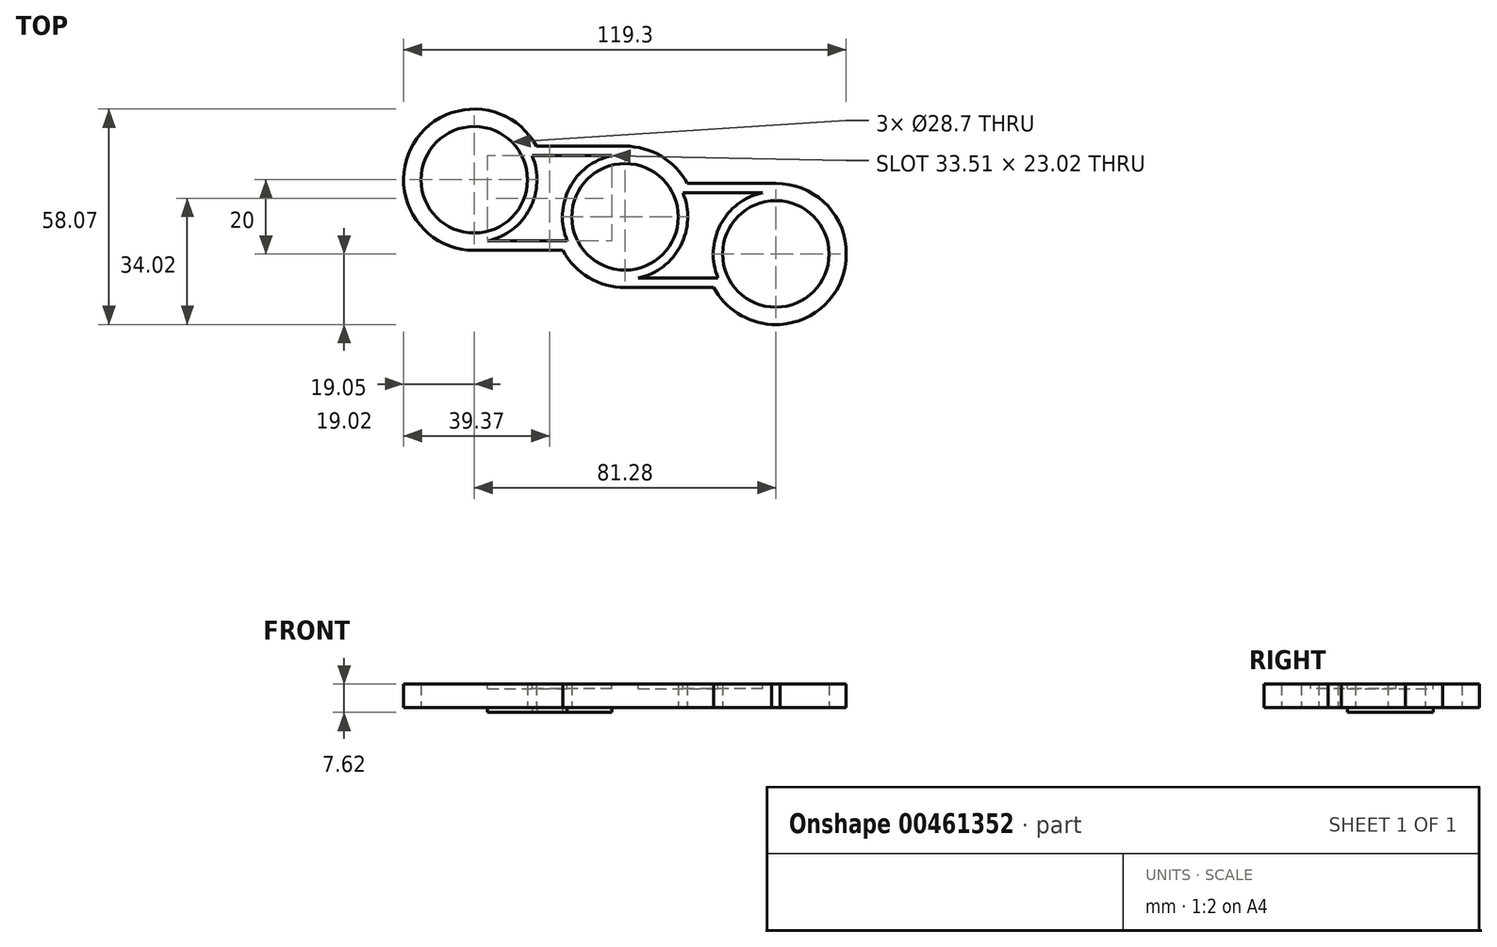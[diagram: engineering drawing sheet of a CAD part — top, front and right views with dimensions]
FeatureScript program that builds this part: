
annotation { "Feature Type Name" : "Feature", "Feature Type Description" : "" }
export const myFeature = defineFeature(function(context is Context, id is Id, definition is map)
    precondition{}
    {
        {
            var Q0;
            Q0=qCreatedBy(makeId("Top.planeOp"),FACE);
            var sketch = newSketch(context, id + "F0", { "sketchPlane" : qUnion([Q0])});
            skCircle(sketch, "E0", {"center": v(0, 0) * mm, "radius": 14.35 * mm});
            skCircle(sketch, "E1", {"center": v(40.64, -10) * mm, "radius": 14.35 * mm});
            skCircle(sketch, "E2", {"center": v(-40.64, 10) * mm, "radius": 14.35 * mm});
            skCircle(sketch, "E3", {"center": v(-40.64, 10) * mm, "radius": 19.05 * mm});
            skCircle(sketch, "E4", {"center": v(0, 0) * mm, "radius": 19.05 * mm});
            skCircle(sketch, "E5", {"center": v(40.64, -10) * mm, "radius": 19.05 * mm});
            skLineSegment(sketch, "E6", {"start": v(0, 19.05) * mm, "end": v(-23.88, 19.05) * mm});
            skLineSegment(sketch, "E7", {"start": v(-40.64, -9.05) * mm, "end": v(-16.76, -9.05) * mm});
            skLineSegment(sketch, "E8", {"start": v(0, -19.05) * mm, "end": v(23.88, -19.05) * mm});
            skLineSegment(sketch, "E9", {"start": v(40.64, 9.05) * mm, "end": v(16.76, 9.05) * mm});
            skLineSegment(sketch, "E10", {"start": v(-59.69, 10.15) * mm, "end": v(-59.69, 55.41) * mm});
            skLineSegment(sketch, "E11", {"start": v(59.6, -11.8) * mm, "end": v(59.6, 49.87) * mm});
            skLineSegment(sketch, "E12", {"start": v(-40.64, 29.05) * mm, "end": v(-1.94, 29.05) * mm});
            skLineSegment(sketch, "E13", {"start": v(41.8, -29.02) * mm, "end": v(-19.86, -29.02) * mm});
            skSolve(sketch);
        }
        {
            var Q0;
            Q0=makeQuery(id+"F0.imprint","IMPRINT",FACE,{"disambiguationData":[TD([[makeQuery(id+"F0.imprint","IMPRINT",EDGE,{"derivedFrom":sQuery(id+"F0.wireOp",EDGE,"E2")}),-1.0]])]});
            var Q1;
            {var subQ0=sQuery(id+"F0.wireOp",EDGE,"E6");Q1=makeQuery(id+"F0.imprint","IMPRINT",FACE,{"disambiguationData":[TD([[makeQuery(id+"F0.imprint","IMPRINT",EDGE,{"derivedFrom":subQ0}),1.0]])]});}
            var Q2;
            Q2=makeQuery(id+"F0.imprint","IMPRINT",FACE,{"disambiguationData":[TD([[makeQuery(id+"F0.imprint","IMPRINT",EDGE,{"derivedFrom":sQuery(id+"F0.wireOp",EDGE,"E0")}),-1.0]])]});
            var Q3;
            {var subQ0=sQuery(id+"F0.wireOp",EDGE,"E8");Q3=makeQuery(id+"F0.imprint","IMPRINT",FACE,{"disambiguationData":[TD([[makeQuery(id+"F0.imprint","IMPRINT",EDGE,{"derivedFrom":subQ0}),1.0]])]});}
            var Q4;
            Q4=makeQuery(id+"F0.imprint","IMPRINT",FACE,{"disambiguationData":[TD([[makeQuery(id+"F0.imprint","IMPRINT",EDGE,{"derivedFrom":sQuery(id+"F0.wireOp",EDGE,"E1")}),-1.0]])]});
            extrude(context, id + "F1", {"entities" : qUnion([Q0, Q1, Q2, Q3, Q4]), "depth" : 7.62 * mm});
        }
        {
            var Q0;
            Q0=makeQuery(id+"F1.opExtrude","CAP_FACE",FACE,{"disambiguationData":[OSD([sQuery(id+"F0.wireOp",EDGE,"E0"),sQuery(id+"F0.wireOp",EDGE,"E1"),sQuery(id+"F0.wireOp",EDGE,"E2"),sQuery(id+"F0.wireOp",EDGE,"E3"),sQuery(id+"F0.wireOp",EDGE,"E4"),sQuery(id+"F0.wireOp",EDGE,"E5"),sQuery(id+"F0.wireOp",EDGE,"E6"),sQuery(id+"F0.wireOp",EDGE,"E7"),sQuery(id+"F0.wireOp",EDGE,"E8"),sQuery(id+"F0.wireOp",EDGE,"E9")])],"isStart":false});
            shell(context, id + "F2", {"entities" : qUnion([Q0]), "thickness" : 2.54 * mm});
        }
        {
            var Q0;
            Q0=makeQuery(id+"F1.opExtrude","CAP_FACE",FACE,{"disambiguationData":[OSD([sQuery(id+"F0.wireOp",EDGE,"E0"),sQuery(id+"F0.wireOp",EDGE,"E1"),sQuery(id+"F0.wireOp",EDGE,"E2"),sQuery(id+"F0.wireOp",EDGE,"E3"),sQuery(id+"F0.wireOp",EDGE,"E4"),sQuery(id+"F0.wireOp",EDGE,"E5"),sQuery(id+"F0.wireOp",EDGE,"E6"),sQuery(id+"F0.wireOp",EDGE,"E7"),sQuery(id+"F0.wireOp",EDGE,"E8"),sQuery(id+"F0.wireOp",EDGE,"E9")])],"isStart":false});
            var sketch = newSketch(context, id + "F3", { "sketchPlane" : qUnion([Q0])});
            skLineSegment(sketch, "E14.0", {"start": v(-3.57, 16.51) * mm, "end": v(-25.05, 16.5) * mm});
            skArc(sketch, "E14.1", {"start": v(-37.07, -6.5) * mm, "mid": v(-25.67, 2.18) * mm, "end": v(-25.05, 16.5) * mm});
            skLineSegment(sketch, "E14.2", {"start": v(-37.07, -6.5) * mm, "end": v(-15.59, -6.5) * mm});
            skArc(sketch, "E14.3", {"start": v(-3.57, 16.51) * mm, "mid": v(-14.97, 7.82) * mm, "end": v(-15.59, -6.5) * mm});
            skLineSegment(sketch, "E14.4", {"start": v(37.07, 6.51) * mm, "end": v(15.59, 6.5) * mm});
            skArc(sketch, "E14.5", {"start": v(3.57, -16.51) * mm, "mid": v(14.97, -7.82) * mm, "end": v(15.59, 6.5) * mm});
            skArc(sketch, "E14.6", {"start": v(37.07, 6.5) * mm, "mid": v(25.67, -2.18) * mm, "end": v(25.05, -16.5) * mm});
            skLineSegment(sketch, "E14.7", {"start": v(3.57, -16.51) * mm, "end": v(25.05, -16.51) * mm});
            skSolve(sketch);
        }
        {
            var Q0;
            Q0 = qSketchRegion(id + "F3", true);
            extrude(context, id + "F4", {"entities" : qUnion([Q0]), "operationType" : NewBodyOperationType.ADD, "oppositeDirection" : true, "depth" : 7.62 * mm});
        }
        {
            var Q0;
            Q0 = qSketchRegion(id + "F3", true);
            extrude(context, id + "F5", {"entities" : qUnion([Q0]), "operationType" : NewBodyOperationType.REMOVE, "oppositeDirection" : true, "depth" : 1.27 * mm});
        }
        {
            var Q0;
            Q0=makeQuery(id+"F1.opExtrude","CAP_FACE",FACE,{"disambiguationData":[OSD([sQuery(id+"F0.wireOp",EDGE,"E0"),sQuery(id+"F0.wireOp",EDGE,"E1"),sQuery(id+"F0.wireOp",EDGE,"E2"),sQuery(id+"F0.wireOp",EDGE,"E3"),sQuery(id+"F0.wireOp",EDGE,"E4"),sQuery(id+"F0.wireOp",EDGE,"E5"),sQuery(id+"F0.wireOp",EDGE,"E6"),sQuery(id+"F0.wireOp",EDGE,"E7"),sQuery(id+"F0.wireOp",EDGE,"E8"),sQuery(id+"F0.wireOp",EDGE,"E9"),sQuery(id+"F0.wireOp",EDGE,"E11"),sQuery(id+"F0.wireOp",EDGE,"E13")])],"isStart":true});
            var sketch = newSketch(context, id + "F6", { "sketchPlane" : qUnion([Q0])});
            skArc(sketch, "E15.0", {"start": v(-37.07, 6.5) * mm, "mid": v(-25.67, -2.18) * mm, "end": v(-25.05, -16.5) * mm});
            skLineSegment(sketch, "E15.1", {"start": v(-37.07, 6.5) * mm, "end": v(-15.59, 6.5) * mm});
            skArc(sketch, "E15.2", {"start": v(-3.57, -16.51) * mm, "mid": v(-14.97, -7.82) * mm, "end": v(-15.59, 6.5) * mm});
            skLineSegment(sketch, "E15.3", {"start": v(-3.57, -16.51) * mm, "end": v(-25.05, -16.5) * mm});
            skLineSegment(sketch, "E15.4", {"start": v(37.07, -6.51) * mm, "end": v(15.59, -6.5) * mm});
            skArc(sketch, "E15.5", {"start": v(3.57, 16.51) * mm, "mid": v(14.97, 7.82) * mm, "end": v(15.59, -6.5) * mm});
            skArc(sketch, "E15.6", {"start": v(37.07, -6.5) * mm, "mid": v(25.67, 2.18) * mm, "end": v(25.05, 16.5) * mm});
            skLineSegment(sketch, "E15.7", {"start": v(3.57, 16.51) * mm, "end": v(25.05, 16.51) * mm});
            skSolve(sketch);
        }
        {
            var Q0;
            Q0=makeQuery(id+"F6.imprint","IMPRINT",FACE,{"disambiguationData":[TD([[makeQuery(id+"F6.imprint","IMPRINT",EDGE,{"derivedFrom":sQuery(id+"F6.wireOp",EDGE,"E15.0")}),1.0]])]});
            var Q1;
            Q1=makeQuery(id+"F6.imprint","IMPRINT",FACE,{"disambiguationData":[TD([[makeQuery(id+"F6.imprint","IMPRINT",EDGE,{"derivedFrom":sQuery(id+"F6.wireOp",EDGE,"E15.4")}),-1.0]])]});
            extrude(context, id + "F7", {"entities" : qUnion([Q0, Q1]), "operationType" : NewBodyOperationType.REMOVE, "oppositeDirection" : true, "depth" : 1.27 * mm});
        }
    });
